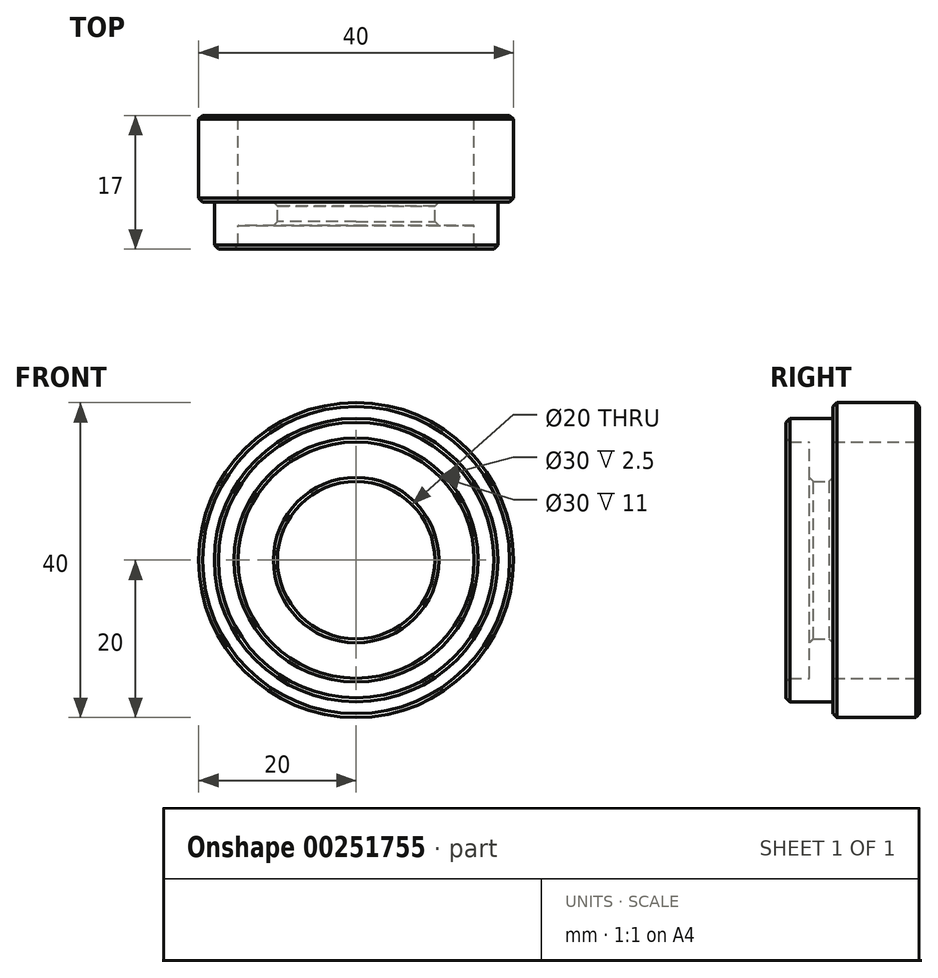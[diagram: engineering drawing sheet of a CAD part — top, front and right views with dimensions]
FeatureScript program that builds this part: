
annotation { "Feature Type Name" : "Feature", "Feature Type Description" : "" }
export const myFeature = defineFeature(function(context is Context, id is Id, definition is map)
    precondition{}
    {
        {
            var Q0;
            Q0=qCreatedBy(makeId("Front.planeOp"),FACE);
            var sketch = newSketch(context, id + "F0", { "sketchPlane" : qUnion([Q0])});
            skCircle(sketch, "E0", {"center": v(0, 0) * mm, "radius": 20 * mm});
            skCircle(sketch, "E1", {"center": v(0, 0) * mm, "radius": 18 * mm});
            skCircle(sketch, "E2", {"center": v(0, 0) * mm, "radius": 15 * mm});
            skCircle(sketch, "E3", {"center": v(0, 0) * mm, "radius": 10 * mm});
            skSolve(sketch);
        }
        {
            var Q0;
            Q0 = qSketchRegion(id + "F0", true);
            extrude(context, id + "F1", {"entities" : qUnion([Q0]), "depth" : 11 * mm});
        }
        {
            var Q0;
            Q0=makeQuery(id+"F0.imprint","IMPRINT",FACE,{"disambiguationData":[TD([[makeQuery(id+"F0.imprint","IMPRINT",EDGE,{"derivedFrom":sQuery(id+"F0.wireOp",EDGE,"E1")}),1.0]])]});
            extrude(context, id + "F2", {"entities" : qUnion([Q0]), "operationType" : NewBodyOperationType.ADD, "depth" : 17 * mm});
        }
        {
            var Q0;
            Q0=makeQuery(id+"F0.imprint","IMPRINT",FACE,{"disambiguationData":[TD([[makeQuery(id+"F0.imprint","IMPRINT",EDGE,{"derivedFrom":sQuery(id+"F0.wireOp",EDGE,"E2")}),1.0]])]});
            extrude(context, id + "F3", {"entities" : qUnion([Q0]), "operationType" : NewBodyOperationType.ADD, "depth" : 14 * mm});
        }
        {
            var Q0;
            {var subQ0=sQuery(id+"F0.wireOp",EDGE,"E2");var subQ1=sQuery(id+"F0.wireOp",EDGE,"E1");Q0=makeQuery(id+"F3.boolean.opBoolean","MERGE",FACE,{"derivedFrom":[makeQuery(id+"F2.boolean.opBoolean","MERGE",FACE,{"derivedFrom":[makeQuery(id+"F1.opExtrude","CAP_FACE",FACE,{"disambiguationData":[OSD([sQuery(id+"F0.wireOp",EDGE,"E0"),subQ1])],"isStart":true}),makeQuery(id+"F2.opExtrude","CAP_FACE",FACE,{"disambiguationData":[OSD([subQ1,subQ0])],"isStart":true})]}),makeQuery(id+"F3.opExtrude","CAP_FACE",FACE,{"disambiguationData":[OSD([subQ0,sQuery(id+"F0.wireOp",EDGE,"E3")])],"isStart":true})]});}
            var sketch = newSketch(context, id + "F4", { "sketchPlane" : qUnion([Q0])});
            skCircle(sketch, "E4", {"center": v(0, 0) * mm, "radius": 15 * mm});
            skSolve(sketch);
        }
        {
            var Q0;
            Q0 = qSketchRegion(id + "F4", true);
            extrude(context, id + "F5", {"entities" : qUnion([Q0]), "operationType" : NewBodyOperationType.REMOVE, "oppositeDirection" : true, "depth" : 11 * mm});
        }
        {
            var Q0;
            Q0=makeQuery(id+"F2.opExtrude","CAP_EDGE",EDGE,{"disambiguationData":[OSD([sQuery(id+"F0.wireOp",EDGE,"E2")])],"isStart":false});
            var Q1;
            Q1=makeQuery(id+"F2.opExtrude","CAP_EDGE",EDGE,{"disambiguationData":[OSD([sQuery(id+"F0.wireOp",EDGE,"E1")])],"isStart":false});
            var Q2;
            Q2=makeQuery(id+"F3.opExtrude","CAP_EDGE",EDGE,{"disambiguationData":[OSD([sQuery(id+"F0.wireOp",EDGE,"E3")])],"isStart":false});
            var Q3;
            Q3=makeQuery(id+"F1.opExtrude","CAP_EDGE",EDGE,{"disambiguationData":[OSD([sQuery(id+"F0.wireOp",EDGE,"E0")])],"isStart":false});
            var Q4;
            Q4=makeQuery(id+"F1.opExtrude","CAP_EDGE",EDGE,{"disambiguationData":[OSD([sQuery(id+"F0.wireOp",EDGE,"E0")])],"isStart":true});
            var Q5;
            Q5=makeQuery(id+"F5.boolean.opBoolean","COPY",EDGE,{"derivedFrom":makeQuery(id+"F5.opExtrude","CAP_EDGE",EDGE,{"disambiguationData":[OSD([sQuery(id+"F4.wireOp",EDGE,"E4")])],"isStart":true})});
            var Q6;
            Q6=makeQuery(id+"F5.boolean.opBoolean","INTERSECT",EDGE,{"derivedFrom":[makeQuery(id+"F3.opExtrude","SWEPT_FACE",FACE,{"disambiguationData":[OSD([sQuery(id+"F0.wireOp",EDGE,"E3")])]}),makeQuery(id+"F5.opExtrude","CAP_FACE",FACE,{"disambiguationData":[OSD([sQuery(id+"F4.wireOp",EDGE,"E4")])],"isStart":false})]});
            chamfer(context, id + "F6", {"entities" : qUnion([Q0, Q1, Q2, Q3, Q4, Q5, Q6]), "chamferType" : ChamferType.OFFSET_ANGLE, "width" : .5 * mm, "oppositeDirection" : false, "angle" : 45 * degree, "tangentPropagation" : true});
        }
    });
